# Revit family: LOROWERK 00603-EF0X
name_source: partatom
category: Rohrformteile
revit_build: Autodesk Revit 2017 (Build: 20160225_1515(x64)
units: mm (PartAtom-declared; Revit-internal decimal feet)

## family parameters
Arbeitsebenenbasiert = Nein
Beim Laden mit Abzugskörper schneiden = Nein
Bemaßung runder Anschluss = Durchmesser verwenden
Gemeinsam genutzt = Nein
Immer vertikal = Ja
Teiletyp = Übergang

## types (2) — shared parameters
BIM = https://media.stage.bim.site
Benennung = LORO-X Übergangsrohr, konzentrisch, DN125/150
Beschreibung = LORO-X Stahlabflussrohre
Bestellmenge (Multiplikator) = 1
Brandschutzklasse = B1 nach DIN 4102
CONNECTOR0_DIAMETER_dZ_0r = 125 mm
CONNECTOR0_dZ_00 = 170 mm
CONNECTOR0_dZ_01 = 250 mm
CONNECTOR0_ref_dZ = 170 mm
CONNECTOR1_DIAMETER_dZ_0r = 150 mm
CONNECTOR1_dZ_01 = 85 mm
CONNECTOR1_ref_dZ = 85 mm
DATANORM = 00603.EF0X
GTIN = 4038088041307
HAN = 00603.EF0X
Hersteller = LOROWERK K.H. Vahlbrauk GmbH & Co. KG
Index = 5
Ist System = Nein
Ist Zubehör = Nein
Nenndruck = 0.5
Nenndrucksystem = PN
Nennweitensystem = DN
Normen/Regeln/Zulassungen = DVGW für Trinkwasser
Produktbezeichnung = LORO-X Stahlabflussrohre
Produktkennung = Formstück
Produktname = LORO-X Übergangsrohre (konzentrische Red.-Stücke)
Produktvideo = https://media.stage.bim.site
Querschnittsform = rund
Typname = LORO-X Übergangsrohre (konzentrische Red.-Stücke)
VDIBSN = 020001???001001???00100100000100300700000000000150000000000000000005
Verbindungsart I = Pressen
Verbindungsart II = axial pressen
Verlegeart = unter Putz
max. zul. Dauer-Betriebstemperatur [Kelvin] = 95

## type names (no varying parameters)
- LORO-X Übergangsrohre (konzentrische Red.-Stücke)
- LOROWERK 00603.EF0X en
